# Revit family: Pivot 1.8
name_source: partatom
category: Lighting Fixtures
units: mm (PartAtom-declared; Revit-internal decimal feet)

## family parameters
Always vertical = No
Cut with Voids When Loaded = No
Light Source = No
OmniClass Number = 23.80.70.00
OmniClass Title = Lighting
Part Type = Normal
Room Calculation Point = Yes
Round Connector Dimension = Use Diameter
Shared = No
Work Plane-Based = No

## types (6) — shared parameters
Apparent Load Phase 1 = 5 W
Base = L&L_Anticorodal aluminium
Body = L&L_Anticorodal aluminium
CRI = -
Code = -
Control system = -
Cutout dimensions = -
Delivered lumen output = 154 lm, R: 43 lm G: 84 lm B: 27 lm (500mA, 33°)
Description = Projector for outdoor applications
Energy efficiency class = A A+ A++
Features = -
Geometry = Pivot 1.8 Movable_A : PIVOT 1.8
H1 = 29 mm  [stored 0.0951444 ft]
IP = IP65
LED Colour = RGB
Length mm = 75 mm
Lens = L&L_Tempered extra-clear glass
Lumen output at source = 201 lm, R: 50 lm G: 111 lm B: 40 lm (500mA)
Manufacturer = L&L Luce&Light
Material = body in anticorodal aluminium,  screen in serigraphed, tempered, transparent extra-clear glass
Model = Pivot 1.8
Mounting = surface mounted (ceiling, wall, ground, spike, strap)
No. and type of led = 3 power LEDs, 50 000h L90 B10 (Ta 25°C)
Notes = with screw to lock in position
Power = max 4,5W
Power Supply = L&L_Steel inox AISI 316L
Power cables = includes 1.50 m PVC cable FROR 6x0.25 Ø4.6 mm
Power supply = max 500mA
Power supply unit = not included
not included
not included
URL = https://www.lucelight.it
URL Accessories and power supply units = https://www.lucelight.it
URL Catalogue = https://www.lucelight.it
URL DXF = https://www.lucelight.it
URL Description = https://www.lucelight.it
URL General code = https://www.lucelight.it
URL IES Photometric file = https://www.lucelight.it
URL Image = https://www.lucelight.it
URL Technical sheet = https://www.lucelight.it
Vertical rotation max = 90.00°
Weight kg = 0.40 kg
Width mm = 40 mm  [stored 0.131234 ft]
Wiring = series
X1 = 100 mm  [stored 0.328084 ft]
zero-valued in all types: Height mm

## per-type parameters (varying)
| type | Light Source | Optics |
| PIVOT 1.8 K 58° (RGB 4.5W 3x500mA) | Light source Pivot : K 58° | 58° |
| PIVOT 1.8 L 45° (RGB 4.5W 3x500mA) | Light source Pivot : L 45° | 45° |
| PIVOT 1.8 M 33° (RGB 4.5W 3x500mA) | Light source Pivot : M 33° | 33° |
| PIVOT 1.8 S 20° (RGB 4.5W 3x500mA) | Light source Pivot : S 20° | 20° |
| PIVOT 1.8 W 22°x46° (RGB 4.5W 3x500mA) | Light source Pivot : W 22°x46° | 22°x46° |
| PIVOT 1.8 X 46°x22° (RGB 4.5W 3x500mA) | Light source Pivot : X 46°x22° | 46°x22° |

note: [stored X ft] marks values corroborated as IEEE doubles in the binary element streams (Revit-internal decimal feet)

## geometry (parser evidence)
native form markers: Blend x2, Sweep x17
no freeform markers — native parametric forms only
